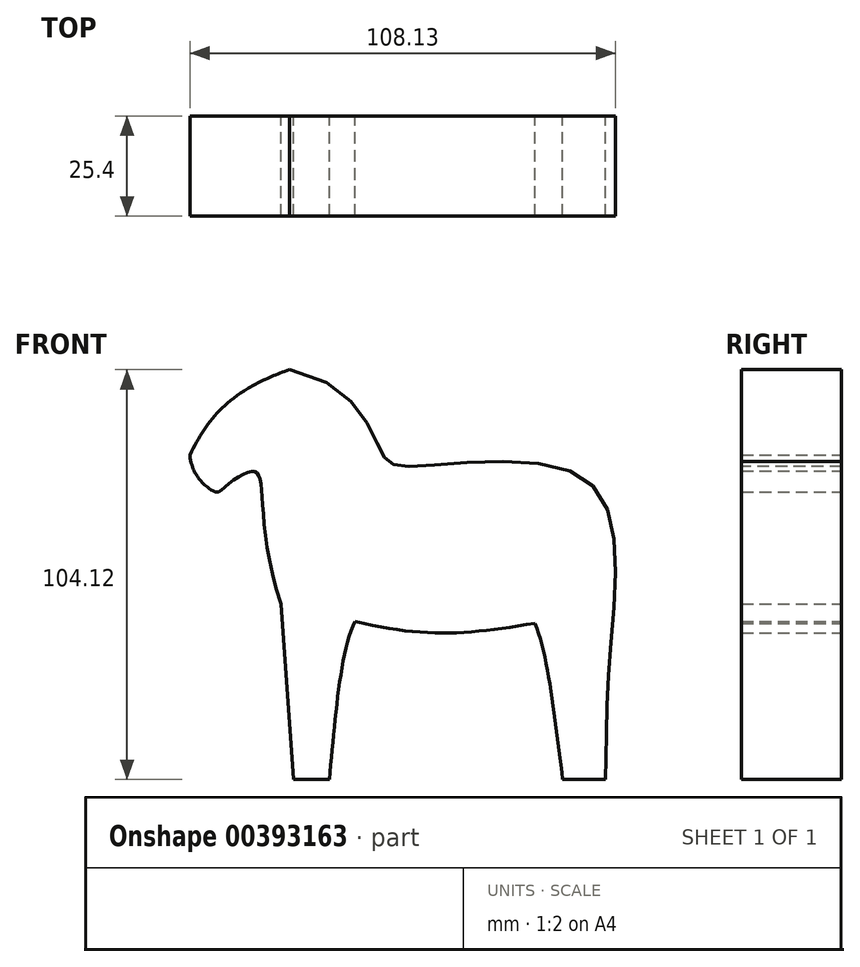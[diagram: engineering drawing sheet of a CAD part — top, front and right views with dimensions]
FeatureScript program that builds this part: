
annotation { "Feature Type Name" : "Feature", "Feature Type Description" : "" }
export const myFeature = defineFeature(function(context is Context, id is Id, definition is map)
    precondition{}
    {
        {
            var Q0;
            Q0=qCreatedBy(makeId("Front.planeOp"),FACE);
            var sketch = newSketch(context, id + "F0", { "sketchPlane" : qUnion([Q0])});
            skPoint(sketch, "E0.middle", {"position": v(0, 0) * mm});
            skLineSegment(sketch, "E1.top", {"start": v(29.46, -60.11) * mm, "end": v(40.37, -60.11) * mm});
            skLineSegment(sketch, "E2.top", {"start": v(-29.83, -60.11) * mm, "end": v(-38.9, -60.11) * mm});
            skLineSegment(sketch, "E2.right", {"start": v(-42.09, -15.48) * mm, "end": v(-38.9, -60.11) * mm});
            skFitSpline(sketch, "E3", {"points": [v(-65.23, 22.36) * mm, v(-63.08, 16.5) * mm, v(-58.15, 12.54) * mm], "startDerivative": vector(1.92, -19.36) * mm, "endDerivative": vector(18.45, -9.4) * mm});
            skFitSpline(sketch, "E4", {"points": [v(-58.15, 12.54) * mm, v(-49.17, 18.2) * mm, v(-42.09, -15.48) * mm], "startDerivative": vector(16.49, 17.07) * mm, "endDerivative": vector(32.32, -95.93) * mm});
            skFitSpline(sketch, "E5", {"points": [v(-23.3, -19.98) * mm, v(22.47, -20.43) * mm], "startDerivative": vector(52.76, -12.85) * mm, "endDerivative": vector(51.4, 8.8) * mm});
            skFitSpline(sketch, "E6", {"points": [v(-29.83, -60.11) * mm, v(-23.3, -19.98) * mm], "startDerivative": vector(4.46, 41.12) * mm, "endDerivative": vector(12.46, 25.87) * mm});
            skFitSpline(sketch, "E7", {"points": [v(29.46, -60.11) * mm, v(22.47, -20.43) * mm], "startDerivative": vector(-5.34, 41.34) * mm, "endDerivative": vector(-10.68, 28.16) * mm});
            skFitSpline(sketch, "E8", {"points": [v(-44.92, 44.65) * mm, v(-16.45, 22.8) * mm, v(-10, 19.4) * mm, v(34.94, 16.36) * mm, v(41.66, -26.05) * mm, v(40.37, -60.11) * mm], "startDerivative": vector(302.09, -22.28) * mm, "endDerivative": vector(-1.18, -116.22) * mm});
            skFitSpline(sketch, "E9", {"points": [v(-65.23, 22.36) * mm, v(-39.33, 44.23) * mm], "startDerivative": vector(13.92, 28.28) * mm, "endDerivative": vector(47.32, 16.15) * mm});
            skLineSegment(sketch, "E10", {"start": v(-51.53, 38.58) * mm, "end": v(-51.53, 49.16) * mm});
            skLineSegment(sketch, "E11", {"start": v(-51.53, 49.16) * mm, "end": v(-44.92, 44.65) * mm});
            skArc(sketch, "E12.filletArc", {"start": v(-59.21, 13.1) * mm, "mid": v(-58.25, 12.9) * mm, "end": v(-57.35, 13.32) * mm});
            skSolve(sketch);
        }
        {
            var Q0;
            Q0=makeQuery(id+"F0.imprint","IMPRINT",FACE,{"disambiguationData":[TD([[makeQuery(id+"F0.imprint","IMPRINT",EDGE,{"derivedFrom":sQuery(id+"F0.wireOp",EDGE,"E1.top")}),1.0]])]});
            extrude(context, id + "F1", {"entities" : qUnion([Q0]), "depth" : 25.4 * mm, "symmetric" : true});
        }
    });
